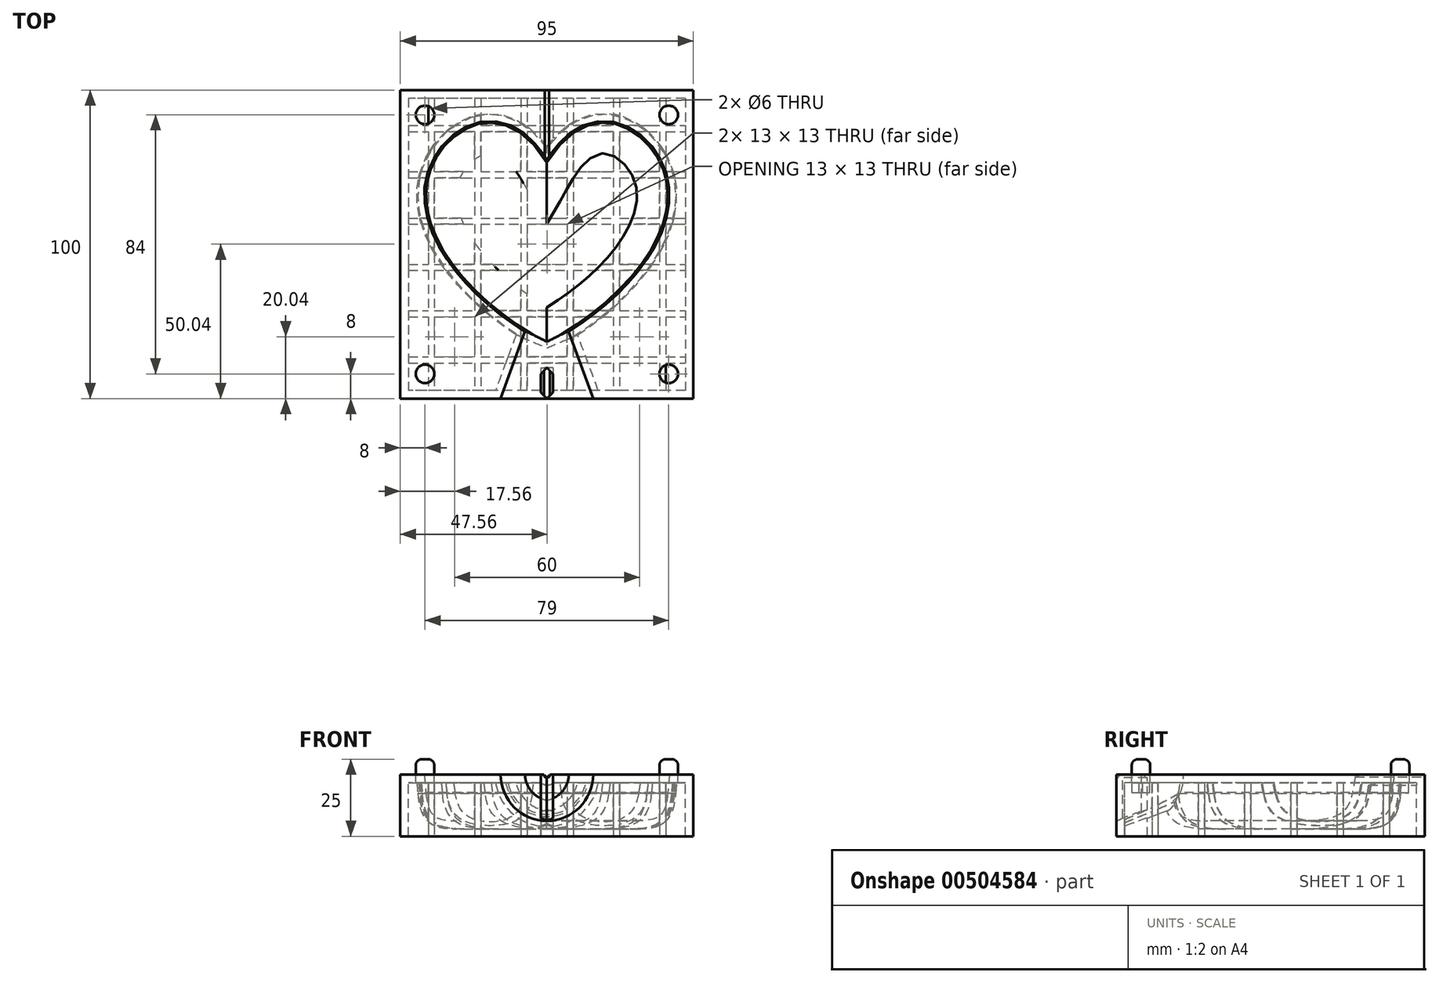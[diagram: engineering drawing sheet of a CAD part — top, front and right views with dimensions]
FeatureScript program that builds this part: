
annotation { "Feature Type Name" : "Feature", "Feature Type Description" : "" }
export const myFeature = defineFeature(function(context is Context, id is Id, definition is map)
    precondition{}
    {
        {
            var Q0;
            Q0=qCreatedBy(makeId("Top.planeOp"),FACE);
            var sketch = newSketch(context, id + "F0", { "sketchPlane" : qUnion([Q0])});
            skLineSegment(sketch, "E0", {"start": v(0, -25) * mm, "end": v(0, -81) * mm});
            skFitSpline(sketch, "E1", {"points": [v(0, -25) * mm, v(37.2, -26.59) * mm, v(0, -81) * mm], "startDerivative": vector(94.86, 165.83) * mm, "endDerivative": vector(-129.77, -70.47) * mm});
            skFitSpline(sketch, "E2.MirrorCS", {"points": [v(0, -25) * mm, v(-37.2, -26.59) * mm, v(0, -81) * mm], "startDerivative": vector(-94.86, 165.83) * mm, "endDerivative": vector(129.77, -70.47) * mm});
            skSolve(sketch);
        }
        {
            var Q0;
            Q0=makeQuery(id+"F0.imprint","IMPRINT",FACE,{"disambiguationData":[TD([[makeQuery(id+"F0.imprint","IMPRINT",EDGE,{"derivedFrom":sQuery(id+"F0.wireOp",EDGE,"E0")}),1.0]])]});
            var Q1;
            Q1=makeQuery(id+"F0.imprint","IMPRINT",FACE,{"disambiguationData":[TD([[makeQuery(id+"F0.imprint","IMPRINT",EDGE,{"derivedFrom":sQuery(id+"F0.wireOp",EDGE,"E0")}),-1.0]])]});
            extrude(context, id + "F1", {"entities" : qUnion([Q0, Q1]), "depth" : 30 * mm, "hasDraft" : true, "draftAngle" : 5 * degree});
        }
        {
            var Q0;
            Q0=makeQuery(id+"F1.opExtrude","CAP_FACE",FACE,{"disambiguationData":[OSD([sQuery(id+"F0.wireOp",EDGE,"E1"),sQuery(id+"F0.wireOp",EDGE,"E2.MirrorCS")])],"isStart":true});
            fillet(context, id + "F2", {"entities" : qUnion([Q0]), "radius" : 10 * mm, "tangentPropagation" : true, "rho" : 0.6, "crossSection" : FilletCrossSection.CONIC, "allowEdgeOverflow" : false});
        }
        {
            var Q0;
            Q0=makeQuery(id+"F1.opExtrude","CAP_FACE",FACE,{"disambiguationData":[OSD([sQuery(id+"F0.wireOp",EDGE,"E1"),sQuery(id+"F0.wireOp",EDGE,"E2.MirrorCS")])],"isStart":false});
            fillet(context, id + "F3", {"entities" : qUnion([Q0]), "radius" : 10 * mm, "tangentPropagation" : true, "rho" : 0.6, "crossSection" : FilletCrossSection.CONIC, "allowEdgeOverflow" : false});
        }
        {
            var Q0;
            Q0=qCreatedBy(makeId("Front.planeOp"),FACE);
            var sketch = newSketch(context, id + "F4", { "sketchPlane" : qUnion([Q0])});
            skCircle(sketch, "E3", {"center": v(0, 15) * mm, "radius": 0.75 * mm});
            skSolve(sketch);
        }
        {
            var Q0;
            Q0=qSketchRegion(id+"F4",true);
            extrude(context, id + "F5", {"entities" : qUnion([Q0]), "operationType" : NewBodyOperationType.ADD, "depth" : 100 * mm});
        }
        {
            var Q0;
            Q0=makeQuery(id+"F5.opExtrude","CAP_FACE",FACE,{"disambiguationData":[OSD([sQuery(id+"F4.wireOp",EDGE,"E3")])],"isStart":false});
            var sketch = newSketch(context, id + "F6", { "sketchPlane" : qUnion([Q0])});
            skCircle(sketch, "E4", {"center": v(0, 15) * mm, "radius": 15 * mm});
            skSolve(sketch);
        }
        {
            var Q0;
            Q0=makeQuery(id+"F6.imprint","IMPRINT",FACE,{"disambiguationData":[TD([[makeQuery(id+"F6.imprint","IMPRINT",EDGE,{"derivedFrom":makeQuery(id+"F5.opExtrude","CAP_EDGE",EDGE,{"disambiguationData":[OSD([sQuery(id+"F4.wireOp",EDGE,"E3")])],"isStart":false})}),1.0]])]});
            var Q1;
            Q1=makeQuery(id+"F6.imprint","IMPRINT",FACE,{"disambiguationData":[TD([[makeQuery(id+"F6.imprint","IMPRINT",EDGE,{"derivedFrom":sQuery(id+"F6.wireOp",EDGE,"E4")}),1.0]])]});
            extrude(context, id + "F7", {"entities" : qUnion([Q0, Q1]), "operationType" : NewBodyOperationType.ADD, "oppositeDirection" : true, "depth" : 60 * mm, "hasDraft" : true, "draftAngle" : 20 * degree, "draftPullDirection" : true});
        }
        {
            var Q0;
            Q0=qCreatedBy(makeId("Top.planeOp"),FACE);
            cPlane(context, id + "F8", {"entities" : qUnion([Q0]), "cplaneType" : CPlaneType.OFFSET, "offset" : 15 * mm, "width" : 150 * mm, "height" : 150 * mm});
        }
        {
            var Q0;
            Q0=qCreatedBy(id+"F8.planeOp",FACE);
            var sketch = newSketch(context, id + "F9", { "sketchPlane" : qUnion([Q0])});
            skLineSegment(sketch, "E5.bottom", {"start": v(47.5, 0) * mm, "end": v(-47.5, 0) * mm});
            skLineSegment(sketch, "E5.top", {"start": v(47.5, -100) * mm, "end": v(-47.5, -100) * mm});
            skLineSegment(sketch, "E5.left", {"start": v(47.5, 0) * mm, "end": v(47.5, -100) * mm});
            skLineSegment(sketch, "E5.right", {"start": v(-47.5, 0) * mm, "end": v(-47.5, -100) * mm});
            skPoint(sketch, "E5.middle", {"position": v(0, -50) * mm});
            skSolve(sketch);
        }
        {
            var Q0;
            Q0=qSketchRegion(id+"F9",true);
            extrude(context, id + "F10", {"entities" : qUnion([Q0]), "oppositeDirection" : true, "depth" : 20 * mm});
        }
        {
            var Q0;
            Q0=makeQuery(id+"F1.opExtrude","SWEPT_BODY",BODY,{"disambiguationData":[OSD([sQuery(id+"F0.wireOp",EDGE,"E1"),sQuery(id+"F0.wireOp",EDGE,"E2.MirrorCS")])]});
            var Q1;
            Q1=makeQuery(id+"F10.opExtrude","SWEPT_BODY",BODY,{"disambiguationData":[OSD([sQuery(id+"F9.wireOp",EDGE,"E5.bottom"),sQuery(id+"F9.wireOp",EDGE,"E5.top"),sQuery(id+"F9.wireOp",EDGE,"E5.left"),sQuery(id+"F9.wireOp",EDGE,"E5.right")])]});
            booleanBodies(context, id + "F11", {"operationType" : BooleanOperationType.SUBTRACTION, "tools" : qUnion([Q0]), "targets" : qUnion([Q1])});
        }
        {
            var Q0;
            Q0=makeQuery(id+"F10.opExtrude","CAP_FACE",FACE,{"disambiguationData":[OSD([sQuery(id+"F9.wireOp",EDGE,"E5.bottom"),sQuery(id+"F9.wireOp",EDGE,"E5.top"),sQuery(id+"F9.wireOp",EDGE,"E5.left"),sQuery(id+"F9.wireOp",EDGE,"E5.right")])],"isStart":false});
            shell(context, id + "F12", {"entities" : qUnion([Q0]), "thickness" : (0.44 * 6) * mm});
        }
        {
            var Q0;
            Q0=makeQuery(id+"F10.opExtrude","CAP_FACE",FACE,{"disambiguationData":[OSD([sQuery(id+"F9.wireOp",EDGE,"E5.bottom"),sQuery(id+"F9.wireOp",EDGE,"E5.top"),sQuery(id+"F9.wireOp",EDGE,"E5.left"),sQuery(id+"F9.wireOp",EDGE,"E5.right")])],"isStart":false});
            var sketch = newSketch(context, id + "F13", { "sketchPlane" : qUnion([Q0])});
            skLineSegment(sketch, "E6.bottom", {"start": v(38.56, 2.64) * mm, "end": v(36.56, 2.64) * mm});
            skLineSegment(sketch, "E6.top", {"start": v(38.56, 97.36) * mm, "end": v(36.56, 97.36) * mm});
            skLineSegment(sketch, "E6.left", {"start": v(38.56, 2.64) * mm, "end": v(38.56, 97.36) * mm});
            skLineSegment(sketch, "E6.right", {"start": v(36.56, 2.64) * mm, "end": v(36.56, 97.36) * mm});
            skLineSegment(sketch, "E7.1.0.0", {"start": v(23.56, 2.64) * mm, "end": v(23.56, 97.36) * mm});
            skLineSegment(sketch, "E7.1.0.1", {"start": v(21.56, 2.64) * mm, "end": v(21.56, 97.36) * mm});
            skLineSegment(sketch, "E7.1.0.2", {"start": v(23.56, 97.36) * mm, "end": v(21.56, 97.36) * mm});
            skLineSegment(sketch, "E7.1.0.3", {"start": v(23.56, 2.64) * mm, "end": v(21.56, 2.64) * mm});
            skLineSegment(sketch, "E7.2.0.0", {"start": v(8.56, 2.64) * mm, "end": v(8.56, 97.36) * mm});
            skLineSegment(sketch, "E7.2.0.1", {"start": v(6.56, 2.64) * mm, "end": v(6.56, 97.36) * mm});
            skLineSegment(sketch, "E7.2.0.2", {"start": v(8.56, 97.36) * mm, "end": v(6.56, 97.36) * mm});
            skLineSegment(sketch, "E7.2.0.3", {"start": v(8.56, 2.64) * mm, "end": v(6.56, 2.64) * mm});
            skLineSegment(sketch, "E7.3.0.0", {"start": v(-6.44, 2.64) * mm, "end": v(-6.44, 97.36) * mm});
            skLineSegment(sketch, "E7.3.0.1", {"start": v(-8.44, 2.64) * mm, "end": v(-8.44, 97.36) * mm});
            skLineSegment(sketch, "E7.3.0.2", {"start": v(-6.44, 97.36) * mm, "end": v(-8.44, 97.36) * mm});
            skLineSegment(sketch, "E7.3.0.3", {"start": v(-6.44, 2.64) * mm, "end": v(-8.44, 2.64) * mm});
            skLineSegment(sketch, "E7.4.0.0", {"start": v(-21.44, 2.64) * mm, "end": v(-21.44, 97.36) * mm});
            skLineSegment(sketch, "E7.4.0.1", {"start": v(-23.44, 2.64) * mm, "end": v(-23.44, 97.36) * mm});
            skLineSegment(sketch, "E7.4.0.2", {"start": v(-21.44, 97.36) * mm, "end": v(-23.44, 97.36) * mm});
            skLineSegment(sketch, "E7.4.0.3", {"start": v(-21.44, 2.64) * mm, "end": v(-23.44, 2.64) * mm});
            skLineSegment(sketch, "E7.5.0.0", {"start": v(-36.44, 2.64) * mm, "end": v(-36.44, 97.36) * mm});
            skLineSegment(sketch, "E7.5.0.1", {"start": v(-38.44, 2.64) * mm, "end": v(-38.44, 97.36) * mm});
            skLineSegment(sketch, "E7.5.0.2", {"start": v(-36.44, 97.36) * mm, "end": v(-38.44, 97.36) * mm});
            skLineSegment(sketch, "E7.5.0.3", {"start": v(-36.44, 2.64) * mm, "end": v(-38.44, 2.64) * mm});
            skLineSegment(sketch, "E7.direction1", {"start": v(36.56, 2.64) * mm, "end": v(21.56, 2.64) * mm, "construction": true});
            skLineSegment(sketch, "E8", {"start": v(-6.44, 2.64) * mm, "end": v(6.56, 2.64) * mm, "construction": true});
            skLineSegment(sketch, "E9.bottom", {"start": v(-44.86, 11.46) * mm, "end": v(-44.86, 13.46) * mm});
            skLineSegment(sketch, "E9.top", {"start": v(44.86, 11.46) * mm, "end": v(44.86, 13.46) * mm});
            skLineSegment(sketch, "E9.left", {"start": v(-44.86, 11.46) * mm, "end": v(44.86, 11.46) * mm});
            skLineSegment(sketch, "E9.right", {"start": v(-44.86, 13.46) * mm, "end": v(44.86, 13.46) * mm});
            skLineSegment(sketch, "E10.1.0.0", {"start": v(-44.86, 26.46) * mm, "end": v(44.86, 26.46) * mm});
            skLineSegment(sketch, "E10.1.0.1", {"start": v(-44.86, 28.46) * mm, "end": v(44.86, 28.46) * mm});
            skLineSegment(sketch, "E10.1.0.2", {"start": v(44.86, 26.46) * mm, "end": v(44.86, 28.46) * mm});
            skLineSegment(sketch, "E10.1.0.3", {"start": v(-44.86, 26.46) * mm, "end": v(-44.86, 28.46) * mm});
            skLineSegment(sketch, "E10.2.0.0", {"start": v(-44.86, 41.46) * mm, "end": v(44.86, 41.46) * mm});
            skLineSegment(sketch, "E10.2.0.1", {"start": v(-44.86, 43.46) * mm, "end": v(44.86, 43.46) * mm});
            skLineSegment(sketch, "E10.2.0.2", {"start": v(44.86, 41.46) * mm, "end": v(44.86, 43.46) * mm});
            skLineSegment(sketch, "E10.2.0.3", {"start": v(-44.86, 41.46) * mm, "end": v(-44.86, 43.46) * mm});
            skLineSegment(sketch, "E10.3.0.0", {"start": v(-44.86, 56.46) * mm, "end": v(44.86, 56.46) * mm});
            skLineSegment(sketch, "E10.3.0.1", {"start": v(-44.86, 58.46) * mm, "end": v(44.86, 58.46) * mm});
            skLineSegment(sketch, "E10.3.0.2", {"start": v(44.86, 56.46) * mm, "end": v(44.86, 58.46) * mm});
            skLineSegment(sketch, "E10.3.0.3", {"start": v(-44.86, 56.46) * mm, "end": v(-44.86, 58.46) * mm});
            skLineSegment(sketch, "E10.4.0.0", {"start": v(-44.86, 71.46) * mm, "end": v(44.86, 71.46) * mm});
            skLineSegment(sketch, "E10.4.0.1", {"start": v(-44.86, 73.46) * mm, "end": v(44.86, 73.46) * mm});
            skLineSegment(sketch, "E10.4.0.2", {"start": v(44.86, 71.46) * mm, "end": v(44.86, 73.46) * mm});
            skLineSegment(sketch, "E10.4.0.3", {"start": v(-44.86, 71.46) * mm, "end": v(-44.86, 73.46) * mm});
            skLineSegment(sketch, "E10.5.0.0", {"start": v(-44.86, 86.46) * mm, "end": v(44.86, 86.46) * mm});
            skLineSegment(sketch, "E10.5.0.1", {"start": v(-44.86, 88.46) * mm, "end": v(44.86, 88.46) * mm});
            skLineSegment(sketch, "E10.5.0.2", {"start": v(44.86, 86.46) * mm, "end": v(44.86, 88.46) * mm});
            skLineSegment(sketch, "E10.5.0.3", {"start": v(-44.86, 86.46) * mm, "end": v(-44.86, 88.46) * mm});
            skLineSegment(sketch, "E10.direction1", {"start": v(-44.86, 13.46) * mm, "end": v(-44.86, 28.46) * mm, "construction": true});
            skLineSegment(sketch, "E11", {"start": v(-44.86, 56.46) * mm, "end": v(-44.86, 43.46) * mm, "construction": true});
            skSolve(sketch);
        }
        {
            var Q0;
            Q0=makeQuery(id+"F13.imprint","IMPRINT",FACE,{"disambiguationData":[TD([[makeQuery(id+"F13.imprint","IMPRINT",EDGE,{"derivedFrom":sQuery(id+"F13.wireOp",EDGE,"E6.bottom")}),-1.0]])]});
            var Q1;
            Q1=makeQuery(id+"F13.imprint","IMPRINT",FACE,{"disambiguationData":[TD([[makeQuery(id+"F13.imprint","IMPRINT",EDGE,{"derivedFrom":sQuery(id+"F13.wireOp",EDGE,"E7.2.0.0")}),1.0]])]});
            var Q2;
            Q2=makeQuery(id+"F13.imprint","IMPRINT",FACE,{"disambiguationData":[TD([[makeQuery(id+"F13.imprint","IMPRINT",EDGE,{"derivedFrom":sQuery(id+"F13.wireOp",EDGE,"E7.3.0.0")}),1.0]])]});
            var Q3;
            Q3=makeQuery(id+"F13.imprint","IMPRINT",FACE,{"disambiguationData":[TD([[makeQuery(id+"F13.imprint","IMPRINT",EDGE,{"derivedFrom":sQuery(id+"F13.wireOp",EDGE,"E7.4.0.0")}),1.0]])]});
            var Q4;
            Q4=makeQuery(id+"F13.imprint","IMPRINT",FACE,{"disambiguationData":[TD([[makeQuery(id+"F13.imprint","IMPRINT",EDGE,{"derivedFrom":sQuery(id+"F13.wireOp",EDGE,"E7.5.0.0")}),1.0]])]});
            var Q5;
            Q5=makeQuery(id+"F13.imprint","IMPRINT",FACE,{"disambiguationData":[TD([[makeQuery(id+"F13.imprint","IMPRINT",EDGE,{"derivedFrom":sQuery(id+"F13.wireOp",EDGE,"E7.1.0.0")}),1.0]])]});
            var Q6;
            {var subQ0=sQuery(id+"F13.wireOp",EDGE,"E9.right");var subQ1=sQuery(id+"F13.wireOp",EDGE,"E6.left");var subQ2=makeQuery(id+"F13.imprint","INTERSECT",VERTEX,{"derivedFrom":[subQ1,subQ0]});Q6=makeQuery(id+"F13.imprint","IMPRINT",FACE,{"disambiguationData":[TD([[makeQuery(id+"F13.imprint","IMPRINT",EDGE,{"disambiguationData":[TD([[subQ2,-1.0]])],"derivedFrom":subQ1}),1.0]])]});}
            var Q7;
            {var subQ0=sQuery(id+"F13.wireOp",EDGE,"E10.1.0.1");var subQ1=sQuery(id+"F13.wireOp",EDGE,"E6.left");var subQ2=makeQuery(id+"F13.imprint","INTERSECT",VERTEX,{"derivedFrom":[subQ1,subQ0]});Q7=makeQuery(id+"F13.imprint","IMPRINT",FACE,{"disambiguationData":[TD([[makeQuery(id+"F13.imprint","IMPRINT",EDGE,{"disambiguationData":[TD([[subQ2,-1.0]])],"derivedFrom":subQ1}),1.0]])]});}
            var Q8;
            {var subQ0=sQuery(id+"F13.wireOp",EDGE,"E10.2.0.1");var subQ1=sQuery(id+"F13.wireOp",EDGE,"E6.left");var subQ2=makeQuery(id+"F13.imprint","INTERSECT",VERTEX,{"derivedFrom":[subQ1,subQ0]});Q8=makeQuery(id+"F13.imprint","IMPRINT",FACE,{"disambiguationData":[TD([[makeQuery(id+"F13.imprint","IMPRINT",EDGE,{"disambiguationData":[TD([[subQ2,-1.0]])],"derivedFrom":subQ1}),1.0]])]});}
            var Q9;
            {var subQ0=sQuery(id+"F13.wireOp",EDGE,"E10.1.0.0");var subQ1=sQuery(id+"F13.wireOp",EDGE,"E6.left");var subQ2=makeQuery(id+"F13.imprint","INTERSECT",VERTEX,{"derivedFrom":[subQ1,subQ0]});Q9=makeQuery(id+"F13.imprint","IMPRINT",FACE,{"disambiguationData":[TD([[makeQuery(id+"F13.imprint","IMPRINT",EDGE,{"disambiguationData":[TD([[subQ2,-1.0]])],"derivedFrom":subQ1}),1.0]])]});}
            var Q10;
            {var subQ0=sQuery(id+"F13.wireOp",EDGE,"E10.2.0.0");var subQ1=sQuery(id+"F13.wireOp",EDGE,"E6.left");var subQ2=makeQuery(id+"F13.imprint","INTERSECT",VERTEX,{"derivedFrom":[subQ1,subQ0]});Q10=makeQuery(id+"F13.imprint","IMPRINT",FACE,{"disambiguationData":[TD([[makeQuery(id+"F13.imprint","IMPRINT",EDGE,{"disambiguationData":[TD([[subQ2,-1.0]])],"derivedFrom":subQ1}),1.0]])]});}
            var Q11;
            {var subQ0=sQuery(id+"F13.wireOp",EDGE,"E10.3.0.0");var subQ1=sQuery(id+"F13.wireOp",EDGE,"E6.left");var subQ2=makeQuery(id+"F13.imprint","INTERSECT",VERTEX,{"derivedFrom":[subQ1,subQ0]});Q11=makeQuery(id+"F13.imprint","IMPRINT",FACE,{"disambiguationData":[TD([[makeQuery(id+"F13.imprint","IMPRINT",EDGE,{"disambiguationData":[TD([[subQ2,-1.0]])],"derivedFrom":subQ1}),1.0]])]});}
            var Q12;
            {var subQ0=sQuery(id+"F13.wireOp",EDGE,"E10.3.0.1");var subQ1=sQuery(id+"F13.wireOp",EDGE,"E6.left");var subQ2=makeQuery(id+"F13.imprint","INTERSECT",VERTEX,{"derivedFrom":[subQ1,subQ0]});Q12=makeQuery(id+"F13.imprint","IMPRINT",FACE,{"disambiguationData":[TD([[makeQuery(id+"F13.imprint","IMPRINT",EDGE,{"disambiguationData":[TD([[subQ2,-1.0]])],"derivedFrom":subQ1}),1.0]])]});}
            var Q13;
            {var subQ0=sQuery(id+"F13.wireOp",EDGE,"E10.4.0.0");var subQ1=sQuery(id+"F13.wireOp",EDGE,"E6.left");var subQ2=makeQuery(id+"F13.imprint","INTERSECT",VERTEX,{"derivedFrom":[subQ1,subQ0]});Q13=makeQuery(id+"F13.imprint","IMPRINT",FACE,{"disambiguationData":[TD([[makeQuery(id+"F13.imprint","IMPRINT",EDGE,{"disambiguationData":[TD([[subQ2,-1.0]])],"derivedFrom":subQ1}),1.0]])]});}
            var Q14;
            {var subQ0=sQuery(id+"F13.wireOp",EDGE,"E10.4.0.1");var subQ1=sQuery(id+"F13.wireOp",EDGE,"E6.left");var subQ2=makeQuery(id+"F13.imprint","INTERSECT",VERTEX,{"derivedFrom":[subQ1,subQ0]});Q14=makeQuery(id+"F13.imprint","IMPRINT",FACE,{"disambiguationData":[TD([[makeQuery(id+"F13.imprint","IMPRINT",EDGE,{"disambiguationData":[TD([[subQ2,-1.0]])],"derivedFrom":subQ1}),1.0]])]});}
            var Q15;
            {var subQ0=sQuery(id+"F13.wireOp",EDGE,"E6.top");Q15=makeQuery(id+"F13.imprint","IMPRINT",FACE,{"disambiguationData":[TD([[makeQuery(id+"F13.imprint","IMPRINT",EDGE,{"derivedFrom":subQ0}),1.0]])]});}
            var Q16;
            {var subQ0=sQuery(id+"F13.wireOp",EDGE,"E10.5.0.0");var subQ1=sQuery(id+"F13.wireOp",EDGE,"E6.left");var subQ2=makeQuery(id+"F13.imprint","INTERSECT",VERTEX,{"derivedFrom":[subQ1,subQ0]});Q16=makeQuery(id+"F13.imprint","IMPRINT",FACE,{"disambiguationData":[TD([[makeQuery(id+"F13.imprint","IMPRINT",EDGE,{"disambiguationData":[TD([[subQ2,-1.0]])],"derivedFrom":subQ1}),1.0]])]});}
            var Q17;
            {var subQ0=sQuery(id+"F13.wireOp",EDGE,"E9.left");var subQ1=sQuery(id+"F13.wireOp",EDGE,"E6.left");var subQ2=makeQuery(id+"F13.imprint","INTERSECT",VERTEX,{"derivedFrom":[subQ1,subQ0]});Q17=makeQuery(id+"F13.imprint","IMPRINT",FACE,{"disambiguationData":[TD([[makeQuery(id+"F13.imprint","IMPRINT",EDGE,{"disambiguationData":[TD([[subQ2,-1.0]])],"derivedFrom":subQ1}),1.0]])]});}
            var Q18;
            {var subQ0=sQuery(id+"F13.wireOp",EDGE,"E9.left");var subQ1=sQuery(id+"F13.wireOp",EDGE,"E6.left");var subQ2=makeQuery(id+"F13.imprint","INTERSECT",VERTEX,{"derivedFrom":[subQ1,subQ0]});Q18=makeQuery(id+"F13.imprint","IMPRINT",FACE,{"disambiguationData":[TD([[makeQuery(id+"F13.imprint","IMPRINT",EDGE,{"disambiguationData":[TD([[subQ2,-1.0]])],"derivedFrom":subQ1}),1.0]])]});}
            var Q19;
            {var subQ5=sQuery(id+"F13.wireOp",EDGE,"E9.top");Q19=makeQuery(id+"F13.imprint","IMPRINT",FACE,{"disambiguationData":[TD([[makeQuery(id+"F13.imprint","IMPRINT",EDGE,{"derivedFrom":subQ5}),1.0]])]});}
            var Q20;
            {var subQ0=sQuery(id+"F13.wireOp",EDGE,"E9.left");var subQ1=sQuery(id+"F13.wireOp",EDGE,"E6.right");var subQ2=makeQuery(id+"F13.imprint","INTERSECT",VERTEX,{"derivedFrom":[subQ1,subQ0]});Q20=makeQuery(id+"F13.imprint","IMPRINT",FACE,{"disambiguationData":[TD([[makeQuery(id+"F13.imprint","IMPRINT",EDGE,{"disambiguationData":[TD([[subQ2,-1.0]])],"derivedFrom":subQ1}),1.0]])]});}
            var Q21;
            {var subQ0=sQuery(id+"F13.wireOp",EDGE,"E9.left");var subQ1=sQuery(id+"F13.wireOp",EDGE,"E7.1.0.1");var subQ2=makeQuery(id+"F13.imprint","INTERSECT",VERTEX,{"derivedFrom":[subQ1,subQ0]});Q21=makeQuery(id+"F13.imprint","IMPRINT",FACE,{"disambiguationData":[TD([[makeQuery(id+"F13.imprint","IMPRINT",EDGE,{"disambiguationData":[TD([[subQ2,-1.0]])],"derivedFrom":subQ1}),1.0]])]});}
            var Q22;
            {var subQ0=sQuery(id+"F13.wireOp",EDGE,"E9.left");var subQ1=sQuery(id+"F13.wireOp",EDGE,"E7.2.0.1");var subQ2=makeQuery(id+"F13.imprint","INTERSECT",VERTEX,{"derivedFrom":[subQ1,subQ0]});Q22=makeQuery(id+"F13.imprint","IMPRINT",FACE,{"disambiguationData":[TD([[makeQuery(id+"F13.imprint","IMPRINT",EDGE,{"disambiguationData":[TD([[subQ2,-1.0]])],"derivedFrom":subQ1}),1.0]])]});}
            var Q23;
            {var subQ0=sQuery(id+"F13.wireOp",EDGE,"E10.3.0.0");var subQ1=sQuery(id+"F13.wireOp",EDGE,"E7.2.0.1");var subQ2=makeQuery(id+"F13.imprint","INTERSECT",VERTEX,{"derivedFrom":[subQ1,subQ0]});Q23=makeQuery(id+"F13.imprint","IMPRINT",FACE,{"disambiguationData":[TD([[makeQuery(id+"F13.imprint","IMPRINT",EDGE,{"disambiguationData":[TD([[subQ2,-1.0]])],"derivedFrom":subQ1}),1.0]])]});}
            var Q24;
            {var subQ0=sQuery(id+"F13.wireOp",EDGE,"E10.3.0.0");var subQ1=sQuery(id+"F13.wireOp",EDGE,"E7.1.0.1");var subQ2=makeQuery(id+"F13.imprint","INTERSECT",VERTEX,{"derivedFrom":[subQ1,subQ0]});Q24=makeQuery(id+"F13.imprint","IMPRINT",FACE,{"disambiguationData":[TD([[makeQuery(id+"F13.imprint","IMPRINT",EDGE,{"disambiguationData":[TD([[subQ2,-1.0]])],"derivedFrom":subQ1}),1.0]])]});}
            var Q25;
            {var subQ0=sQuery(id+"F13.wireOp",EDGE,"E10.2.0.0");var subQ1=sQuery(id+"F13.wireOp",EDGE,"E7.1.0.1");var subQ2=makeQuery(id+"F13.imprint","INTERSECT",VERTEX,{"derivedFrom":[subQ1,subQ0]});Q25=makeQuery(id+"F13.imprint","IMPRINT",FACE,{"disambiguationData":[TD([[makeQuery(id+"F13.imprint","IMPRINT",EDGE,{"disambiguationData":[TD([[subQ2,-1.0]])],"derivedFrom":subQ1}),1.0]])]});}
            var Q26;
            {var subQ0=sQuery(id+"F13.wireOp",EDGE,"E10.1.0.0");var subQ1=sQuery(id+"F13.wireOp",EDGE,"E7.1.0.1");var subQ2=makeQuery(id+"F13.imprint","INTERSECT",VERTEX,{"derivedFrom":[subQ1,subQ0]});Q26=makeQuery(id+"F13.imprint","IMPRINT",FACE,{"disambiguationData":[TD([[makeQuery(id+"F13.imprint","IMPRINT",EDGE,{"disambiguationData":[TD([[subQ2,-1.0]])],"derivedFrom":subQ1}),1.0]])]});}
            var Q27;
            {var subQ0=sQuery(id+"F13.wireOp",EDGE,"E10.1.0.0");var subQ1=sQuery(id+"F13.wireOp",EDGE,"E6.right");var subQ2=makeQuery(id+"F13.imprint","INTERSECT",VERTEX,{"derivedFrom":[subQ1,subQ0]});Q27=makeQuery(id+"F13.imprint","IMPRINT",FACE,{"disambiguationData":[TD([[makeQuery(id+"F13.imprint","IMPRINT",EDGE,{"disambiguationData":[TD([[subQ2,-1.0]])],"derivedFrom":subQ1}),1.0]])]});}
            var Q28;
            {var subQ0=sQuery(id+"F13.wireOp",EDGE,"E10.2.0.0");var subQ1=sQuery(id+"F13.wireOp",EDGE,"E6.right");var subQ2=makeQuery(id+"F13.imprint","INTERSECT",VERTEX,{"derivedFrom":[subQ1,subQ0]});Q28=makeQuery(id+"F13.imprint","IMPRINT",FACE,{"disambiguationData":[TD([[makeQuery(id+"F13.imprint","IMPRINT",EDGE,{"disambiguationData":[TD([[subQ2,-1.0]])],"derivedFrom":subQ1}),1.0]])]});}
            var Q29;
            {var subQ5=sQuery(id+"F13.wireOp",EDGE,"E10.2.0.2");Q29=makeQuery(id+"F13.imprint","IMPRINT",FACE,{"disambiguationData":[TD([[makeQuery(id+"F13.imprint","IMPRINT",EDGE,{"derivedFrom":subQ5}),1.0]])]});}
            var Q30;
            {var subQ5=sQuery(id+"F13.wireOp",EDGE,"E10.3.0.2");Q30=makeQuery(id+"F13.imprint","IMPRINT",FACE,{"disambiguationData":[TD([[makeQuery(id+"F13.imprint","IMPRINT",EDGE,{"derivedFrom":subQ5}),1.0]])]});}
            var Q31;
            {var subQ0=sQuery(id+"F13.wireOp",EDGE,"E10.3.0.0");var subQ1=sQuery(id+"F13.wireOp",EDGE,"E6.right");var subQ2=makeQuery(id+"F13.imprint","INTERSECT",VERTEX,{"derivedFrom":[subQ1,subQ0]});Q31=makeQuery(id+"F13.imprint","IMPRINT",FACE,{"disambiguationData":[TD([[makeQuery(id+"F13.imprint","IMPRINT",EDGE,{"disambiguationData":[TD([[subQ2,-1.0]])],"derivedFrom":subQ1}),1.0]])]});}
            var Q32;
            {var subQ0=sQuery(id+"F13.wireOp",EDGE,"E9.left");var subQ1=sQuery(id+"F13.wireOp",EDGE,"E7.4.0.1");var subQ2=makeQuery(id+"F13.imprint","INTERSECT",VERTEX,{"derivedFrom":[subQ1,subQ0]});Q32=makeQuery(id+"F13.imprint","IMPRINT",FACE,{"disambiguationData":[TD([[makeQuery(id+"F13.imprint","IMPRINT",EDGE,{"disambiguationData":[TD([[subQ2,-1.0]])],"derivedFrom":subQ1}),1.0]])]});}
            var Q33;
            {var subQ5=sQuery(id+"F13.wireOp",EDGE,"E9.bottom");Q33=makeQuery(id+"F13.imprint","IMPRINT",FACE,{"disambiguationData":[TD([[makeQuery(id+"F13.imprint","IMPRINT",EDGE,{"derivedFrom":subQ5}),-1.0]])]});}
            var Q34;
            {var subQ0=sQuery(id+"F13.wireOp",EDGE,"E9.left");var subQ1=sQuery(id+"F13.wireOp",EDGE,"E7.3.0.1");var subQ2=makeQuery(id+"F13.imprint","INTERSECT",VERTEX,{"derivedFrom":[subQ1,subQ0]});Q34=makeQuery(id+"F13.imprint","IMPRINT",FACE,{"disambiguationData":[TD([[makeQuery(id+"F13.imprint","IMPRINT",EDGE,{"disambiguationData":[TD([[subQ2,-1.0]])],"derivedFrom":subQ1}),1.0]])]});}
            var Q35;
            {var subQ0=sQuery(id+"F13.wireOp",EDGE,"E10.1.0.0");var subQ1=sQuery(id+"F13.wireOp",EDGE,"E7.3.0.1");var subQ2=makeQuery(id+"F13.imprint","INTERSECT",VERTEX,{"derivedFrom":[subQ1,subQ0]});Q35=makeQuery(id+"F13.imprint","IMPRINT",FACE,{"disambiguationData":[TD([[makeQuery(id+"F13.imprint","IMPRINT",EDGE,{"disambiguationData":[TD([[subQ2,-1.0]])],"derivedFrom":subQ1}),1.0]])]});}
            var Q36;
            {var subQ0=sQuery(id+"F13.wireOp",EDGE,"E10.1.0.0");var subQ1=sQuery(id+"F13.wireOp",EDGE,"E7.4.0.1");var subQ2=makeQuery(id+"F13.imprint","INTERSECT",VERTEX,{"derivedFrom":[subQ1,subQ0]});Q36=makeQuery(id+"F13.imprint","IMPRINT",FACE,{"disambiguationData":[TD([[makeQuery(id+"F13.imprint","IMPRINT",EDGE,{"disambiguationData":[TD([[subQ2,-1.0]])],"derivedFrom":subQ1}),1.0]])]});}
            var Q37;
            {var subQ5=sQuery(id+"F13.wireOp",EDGE,"E10.1.0.3");Q37=makeQuery(id+"F13.imprint","IMPRINT",FACE,{"disambiguationData":[TD([[makeQuery(id+"F13.imprint","IMPRINT",EDGE,{"derivedFrom":subQ5}),-1.0]])]});}
            var Q38;
            {var subQ5=sQuery(id+"F13.wireOp",EDGE,"E10.2.0.3");Q38=makeQuery(id+"F13.imprint","IMPRINT",FACE,{"disambiguationData":[TD([[makeQuery(id+"F13.imprint","IMPRINT",EDGE,{"derivedFrom":subQ5}),-1.0]])]});}
            var Q39;
            {var subQ0=sQuery(id+"F13.wireOp",EDGE,"E10.2.0.0");var subQ1=sQuery(id+"F13.wireOp",EDGE,"E7.4.0.1");var subQ2=makeQuery(id+"F13.imprint","INTERSECT",VERTEX,{"derivedFrom":[subQ1,subQ0]});Q39=makeQuery(id+"F13.imprint","IMPRINT",FACE,{"disambiguationData":[TD([[makeQuery(id+"F13.imprint","IMPRINT",EDGE,{"disambiguationData":[TD([[subQ2,-1.0]])],"derivedFrom":subQ1}),1.0]])]});}
            var Q40;
            {var subQ0=sQuery(id+"F13.wireOp",EDGE,"E10.2.0.0");var subQ1=sQuery(id+"F13.wireOp",EDGE,"E7.3.0.1");var subQ2=makeQuery(id+"F13.imprint","INTERSECT",VERTEX,{"derivedFrom":[subQ1,subQ0]});Q40=makeQuery(id+"F13.imprint","IMPRINT",FACE,{"disambiguationData":[TD([[makeQuery(id+"F13.imprint","IMPRINT",EDGE,{"disambiguationData":[TD([[subQ2,-1.0]])],"derivedFrom":subQ1}),1.0]])]});}
            var Q41;
            {var subQ0=sQuery(id+"F13.wireOp",EDGE,"E10.1.0.0");var subQ1=sQuery(id+"F13.wireOp",EDGE,"E7.2.0.1");var subQ2=makeQuery(id+"F13.imprint","INTERSECT",VERTEX,{"derivedFrom":[subQ1,subQ0]});Q41=makeQuery(id+"F13.imprint","IMPRINT",FACE,{"disambiguationData":[TD([[makeQuery(id+"F13.imprint","IMPRINT",EDGE,{"disambiguationData":[TD([[subQ2,-1.0]])],"derivedFrom":subQ1}),1.0]])]});}
            var Q42;
            {var subQ0=sQuery(id+"F13.wireOp",EDGE,"E10.2.0.0");var subQ1=sQuery(id+"F13.wireOp",EDGE,"E7.2.0.1");var subQ2=makeQuery(id+"F13.imprint","INTERSECT",VERTEX,{"derivedFrom":[subQ1,subQ0]});Q42=makeQuery(id+"F13.imprint","IMPRINT",FACE,{"disambiguationData":[TD([[makeQuery(id+"F13.imprint","IMPRINT",EDGE,{"disambiguationData":[TD([[subQ2,-1.0]])],"derivedFrom":subQ1}),1.0]])]});}
            var Q43;
            {var subQ0=sQuery(id+"F13.wireOp",EDGE,"E10.4.0.0");var subQ1=sQuery(id+"F13.wireOp",EDGE,"E7.2.0.1");var subQ2=makeQuery(id+"F13.imprint","INTERSECT",VERTEX,{"derivedFrom":[subQ1,subQ0]});Q43=makeQuery(id+"F13.imprint","IMPRINT",FACE,{"disambiguationData":[TD([[makeQuery(id+"F13.imprint","IMPRINT",EDGE,{"disambiguationData":[TD([[subQ2,-1.0]])],"derivedFrom":subQ1}),1.0]])]});}
            var Q44;
            {var subQ0=sQuery(id+"F13.wireOp",EDGE,"E10.4.0.0");var subQ1=sQuery(id+"F13.wireOp",EDGE,"E7.1.0.1");var subQ2=makeQuery(id+"F13.imprint","INTERSECT",VERTEX,{"derivedFrom":[subQ1,subQ0]});Q44=makeQuery(id+"F13.imprint","IMPRINT",FACE,{"disambiguationData":[TD([[makeQuery(id+"F13.imprint","IMPRINT",EDGE,{"disambiguationData":[TD([[subQ2,-1.0]])],"derivedFrom":subQ1}),1.0]])]});}
            var Q45;
            {var subQ0=sQuery(id+"F13.wireOp",EDGE,"E10.4.0.0");var subQ1=sQuery(id+"F13.wireOp",EDGE,"E6.right");var subQ2=makeQuery(id+"F13.imprint","INTERSECT",VERTEX,{"derivedFrom":[subQ1,subQ0]});Q45=makeQuery(id+"F13.imprint","IMPRINT",FACE,{"disambiguationData":[TD([[makeQuery(id+"F13.imprint","IMPRINT",EDGE,{"disambiguationData":[TD([[subQ2,-1.0]])],"derivedFrom":subQ1}),1.0]])]});}
            var Q46;
            {var subQ5=sQuery(id+"F13.wireOp",EDGE,"E10.4.0.2");Q46=makeQuery(id+"F13.imprint","IMPRINT",FACE,{"disambiguationData":[TD([[makeQuery(id+"F13.imprint","IMPRINT",EDGE,{"derivedFrom":subQ5}),1.0]])]});}
            var Q47;
            {var subQ5=sQuery(id+"F13.wireOp",EDGE,"E10.5.0.2");Q47=makeQuery(id+"F13.imprint","IMPRINT",FACE,{"disambiguationData":[TD([[makeQuery(id+"F13.imprint","IMPRINT",EDGE,{"derivedFrom":subQ5}),1.0]])]});}
            var Q48;
            {var subQ0=sQuery(id+"F13.wireOp",EDGE,"E10.5.0.0");var subQ1=sQuery(id+"F13.wireOp",EDGE,"E6.right");var subQ2=makeQuery(id+"F13.imprint","INTERSECT",VERTEX,{"derivedFrom":[subQ1,subQ0]});Q48=makeQuery(id+"F13.imprint","IMPRINT",FACE,{"disambiguationData":[TD([[makeQuery(id+"F13.imprint","IMPRINT",EDGE,{"disambiguationData":[TD([[subQ2,-1.0]])],"derivedFrom":subQ1}),1.0]])]});}
            var Q49;
            {var subQ0=sQuery(id+"F13.wireOp",EDGE,"E10.5.0.0");var subQ1=sQuery(id+"F13.wireOp",EDGE,"E7.1.0.1");var subQ2=makeQuery(id+"F13.imprint","INTERSECT",VERTEX,{"derivedFrom":[subQ1,subQ0]});Q49=makeQuery(id+"F13.imprint","IMPRINT",FACE,{"disambiguationData":[TD([[makeQuery(id+"F13.imprint","IMPRINT",EDGE,{"disambiguationData":[TD([[subQ2,-1.0]])],"derivedFrom":subQ1}),1.0]])]});}
            var Q50;
            {var subQ5=sQuery(id+"F13.wireOp",EDGE,"E10.3.0.3");Q50=makeQuery(id+"F13.imprint","IMPRINT",FACE,{"disambiguationData":[TD([[makeQuery(id+"F13.imprint","IMPRINT",EDGE,{"derivedFrom":subQ5}),-1.0]])]});}
            var Q51;
            {var subQ5=sQuery(id+"F13.wireOp",EDGE,"E10.4.0.3");Q51=makeQuery(id+"F13.imprint","IMPRINT",FACE,{"disambiguationData":[TD([[makeQuery(id+"F13.imprint","IMPRINT",EDGE,{"derivedFrom":subQ5}),-1.0]])]});}
            var Q52;
            {var subQ5=sQuery(id+"F13.wireOp",EDGE,"E10.5.0.3");Q52=makeQuery(id+"F13.imprint","IMPRINT",FACE,{"disambiguationData":[TD([[makeQuery(id+"F13.imprint","IMPRINT",EDGE,{"derivedFrom":subQ5}),-1.0]])]});}
            var Q53;
            {var subQ0=sQuery(id+"F13.wireOp",EDGE,"E10.5.0.0");var subQ1=sQuery(id+"F13.wireOp",EDGE,"E7.4.0.1");var subQ2=makeQuery(id+"F13.imprint","INTERSECT",VERTEX,{"derivedFrom":[subQ1,subQ0]});Q53=makeQuery(id+"F13.imprint","IMPRINT",FACE,{"disambiguationData":[TD([[makeQuery(id+"F13.imprint","IMPRINT",EDGE,{"disambiguationData":[TD([[subQ2,-1.0]])],"derivedFrom":subQ1}),1.0]])]});}
            var Q54;
            {var subQ0=sQuery(id+"F13.wireOp",EDGE,"E10.5.0.0");var subQ1=sQuery(id+"F13.wireOp",EDGE,"E7.3.0.1");var subQ2=makeQuery(id+"F13.imprint","INTERSECT",VERTEX,{"derivedFrom":[subQ1,subQ0]});Q54=makeQuery(id+"F13.imprint","IMPRINT",FACE,{"disambiguationData":[TD([[makeQuery(id+"F13.imprint","IMPRINT",EDGE,{"disambiguationData":[TD([[subQ2,-1.0]])],"derivedFrom":subQ1}),1.0]])]});}
            var Q55;
            {var subQ0=sQuery(id+"F13.wireOp",EDGE,"E10.5.0.0");var subQ1=sQuery(id+"F13.wireOp",EDGE,"E7.2.0.1");var subQ2=makeQuery(id+"F13.imprint","INTERSECT",VERTEX,{"derivedFrom":[subQ1,subQ0]});Q55=makeQuery(id+"F13.imprint","IMPRINT",FACE,{"disambiguationData":[TD([[makeQuery(id+"F13.imprint","IMPRINT",EDGE,{"disambiguationData":[TD([[subQ2,-1.0]])],"derivedFrom":subQ1}),1.0]])]});}
            var Q56;
            {var subQ0=sQuery(id+"F13.wireOp",EDGE,"E10.4.0.0");var subQ1=sQuery(id+"F13.wireOp",EDGE,"E7.3.0.1");var subQ2=makeQuery(id+"F13.imprint","INTERSECT",VERTEX,{"derivedFrom":[subQ1,subQ0]});Q56=makeQuery(id+"F13.imprint","IMPRINT",FACE,{"disambiguationData":[TD([[makeQuery(id+"F13.imprint","IMPRINT",EDGE,{"disambiguationData":[TD([[subQ2,-1.0]])],"derivedFrom":subQ1}),1.0]])]});}
            var Q57;
            {var subQ0=sQuery(id+"F13.wireOp",EDGE,"E10.4.0.0");var subQ1=sQuery(id+"F13.wireOp",EDGE,"E7.4.0.1");var subQ2=makeQuery(id+"F13.imprint","INTERSECT",VERTEX,{"derivedFrom":[subQ1,subQ0]});Q57=makeQuery(id+"F13.imprint","IMPRINT",FACE,{"disambiguationData":[TD([[makeQuery(id+"F13.imprint","IMPRINT",EDGE,{"disambiguationData":[TD([[subQ2,-1.0]])],"derivedFrom":subQ1}),1.0]])]});}
            var Q58;
            {var subQ0=sQuery(id+"F13.wireOp",EDGE,"E10.3.0.0");var subQ1=sQuery(id+"F13.wireOp",EDGE,"E7.4.0.1");var subQ2=makeQuery(id+"F13.imprint","INTERSECT",VERTEX,{"derivedFrom":[subQ1,subQ0]});Q58=makeQuery(id+"F13.imprint","IMPRINT",FACE,{"disambiguationData":[TD([[makeQuery(id+"F13.imprint","IMPRINT",EDGE,{"disambiguationData":[TD([[subQ2,-1.0]])],"derivedFrom":subQ1}),1.0]])]});}
            var Q59;
            {var subQ0=sQuery(id+"F13.wireOp",EDGE,"E10.3.0.0");var subQ1=sQuery(id+"F13.wireOp",EDGE,"E7.3.0.1");var subQ2=makeQuery(id+"F13.imprint","INTERSECT",VERTEX,{"derivedFrom":[subQ1,subQ0]});Q59=makeQuery(id+"F13.imprint","IMPRINT",FACE,{"disambiguationData":[TD([[makeQuery(id+"F13.imprint","IMPRINT",EDGE,{"disambiguationData":[TD([[subQ2,-1.0]])],"derivedFrom":subQ1}),1.0]])]});}
            var Q60;
            {var subQ5=sQuery(id+"F13.wireOp",EDGE,"E10.1.0.2");Q60=makeQuery(id+"F13.imprint","IMPRINT",FACE,{"disambiguationData":[TD([[makeQuery(id+"F13.imprint","IMPRINT",EDGE,{"derivedFrom":subQ5}),1.0]])]});}
            extrude(context, id + "F14", {"entities" : qUnion([Q0, Q1, Q2, Q3, Q4, Q5, Q6, Q7, Q8, Q9, Q10, Q11, Q12, Q13, Q14, Q15, Q16, Q17, Q18, Q19, Q20, Q21, Q22, Q23, Q24, Q25, Q26, Q27, Q28, Q29, Q30, Q31, Q32, Q33, Q34, Q35, Q36, Q37, Q38, Q39, Q40, Q41, Q42, Q43, Q44, Q45, Q46, Q47, Q48, Q49, Q50, Q51, Q52, Q53, Q54, Q55, Q56, Q57, Q58, Q59, Q60]), "endBound" : BoundingType.UP_TO_NEXT, "oppositeDirection" : true, "depth" : 25 * mm});
        }
        {
            var Q0;
            {var subQ0=sQuery(id+"F9.wireOp",EDGE,"E5.bottom");var subQ1=sQuery(id+"F9.wireOp",EDGE,"E5.top");var subQ2=sQuery(id+"F9.wireOp",EDGE,"E5.right");Q0=makeQuery(id+"F11.opBoolean","SPLIT",FACE,{"disambiguationData":[TD([makeQuery(id+"F1.opExtrude","SWEPT_FACE",FACE,{"disambiguationData":[OSD([sQuery(id+"F0.wireOp",EDGE,"E2.MirrorCS")])]})])],"derivedFrom":makeQuery(id+"F10.opExtrude","CAP_FACE",FACE,{"disambiguationData":[OSD([subQ0,subQ1,sQuery(id+"F9.wireOp",EDGE,"E5.left"),subQ2])],"isStart":true})});}
            var sketch = newSketch(context, id + "F15", { "sketchPlane" : qUnion([Q0])});
            skCircle(sketch, "E12", {"center": v(-39.5, -8) * mm, "radius": 3 * mm});
            skCircle(sketch, "E13", {"center": v(39.5, -8) * mm, "radius": 3 * mm});
            skCircle(sketch, "E14", {"center": v(39.5, -92) * mm, "radius": 3 * mm});
            skCircle(sketch, "E15", {"center": v(-39.5, -92) * mm, "radius": 3 * mm});
            skSolve(sketch);
        }
        {
            var Q0;
            Q0=makeQuery(id+"F15.imprint","IMPRINT",FACE,{"disambiguationData":[TD([[makeQuery(id+"F15.imprint","IMPRINT",EDGE,{"derivedFrom":sQuery(id+"F15.wireOp",EDGE,"E13")}),1.0]])]});
            var Q1;
            Q1=makeQuery(id+"F15.imprint","IMPRINT",FACE,{"disambiguationData":[TD([[makeQuery(id+"F15.imprint","IMPRINT",EDGE,{"derivedFrom":sQuery(id+"F15.wireOp",EDGE,"E15")}),1.0]])]});
            extrude(context, id + "F16", {"entities" : qUnion([Q0, Q1]), "operationType" : NewBodyOperationType.ADD, "depth" : 5 * mm});
        }
        {
            var Q0;
            Q0=makeQuery(id+"F15.imprint","IMPRINT",FACE,{"disambiguationData":[TD([[makeQuery(id+"F15.imprint","IMPRINT",EDGE,{"derivedFrom":sQuery(id+"F15.wireOp",EDGE,"E14")}),1.0]])]});
            var Q1;
            Q1=makeQuery(id+"F15.imprint","IMPRINT",FACE,{"disambiguationData":[TD([[makeQuery(id+"F15.imprint","IMPRINT",EDGE,{"derivedFrom":sQuery(id+"F15.wireOp",EDGE,"E12")}),1.0]])]});
            extrude(context, id + "F17", {"entities" : qUnion([Q0, Q1]), "operationType" : NewBodyOperationType.REMOVE, "oppositeDirection" : true, "depth" : 6 * mm});
        }
        {
            var Q0;
            Q0=makeQuery(id+"F16.opExtrude","CAP_EDGE",EDGE,{"disambiguationData":[OSD([sQuery(id+"F15.wireOp",EDGE,"E15")])],"isStart":false});
            fillet(context, id + "F18", {"entities" : qUnion([Q0]), "radius" : 2 * mm, "tangentPropagation" : true, "allowEdgeOverflow" : false});
        }
        {
            var Q0;
            Q0=makeQuery(id+"F16.opExtrude","CAP_EDGE",EDGE,{"disambiguationData":[OSD([sQuery(id+"F15.wireOp",EDGE,"E13")])],"isStart":false});
            fillet(context, id + "F19", {"entities" : qUnion([Q0]), "radius" : 2 * mm, "tangentPropagation" : true, "allowEdgeOverflow" : false});
        }
        {
            var Q0;
            Q0=makeQuery(id+"F10.opExtrude","SWEPT_FACE",FACE,{"disambiguationData":[OSD([sQuery(id+"F9.wireOp",EDGE,"E5.top")])]});
            var sketch = newSketch(context, id + "F20", { "sketchPlane" : qUnion([Q0])});
            skLineSegment(sketch, "E16.bottom", {"start": v(-2, -5) * mm, "end": v(2, -5) * mm});
            skLineSegment(sketch, "E16.top", {"start": v(-2, 35) * mm, "end": v(2, 35) * mm});
            skLineSegment(sketch, "E16.left", {"start": v(-2, -5) * mm, "end": v(-2, 15) * mm});
            skLineSegment(sketch, "E16.right", {"start": v(2, -5) * mm, "end": v(2, 15) * mm});
            skPoint(sketch, "E16.middle", {"position": v(0, 15) * mm});
            skLineSegment(sketch, "E17", {"start": v(2, 15) * mm, "end": v(-2, 15) * mm, "construction": true});
            skArc(sketch, "E18", {"start": v(-1, 15) * mm, "mid": v(0, 14) * mm, "end": v(1, 15) * mm});
            skLineSegment(sketch, "E19", {"start": v(2, 15) * mm, "end": v(1, 15) * mm});
            skLineSegment(sketch, "E20", {"start": v(-2, 15) * mm, "end": v(-1, 15) * mm});
            skSolve(sketch);
        }
        {
            var Q0;
            Q0 = qSketchRegion(id + "F20", true);
            extrude(context, id + "F21", {"entities" : qUnion([Q0]), "operationType" : NewBodyOperationType.ADD, "oppositeDirection" : true, "depth" : 10 * mm});
        }
        {
            var Q0;
            Q0=makeQuery(id+"F21.opExtrude","CAP_EDGE",EDGE,{"disambiguationData":[OSD([sQuery(id+"F20.wireOp",EDGE,"E16.right")])],"isStart":true});
            var Q1;
            Q1=makeQuery(id+"F21.opExtrude","CAP_EDGE",EDGE,{"disambiguationData":[OSD([sQuery(id+"F20.wireOp",EDGE,"E16.left")])],"isStart":true});
            chamfer(context, id + "F22", {"entities" : qUnion([Q0, Q1]), "width" : 2 * mm, "tangentPropagation" : true});
        }
        {
            var Q0;
            {var subQ1=sQuery(id+"F20.wireOp",EDGE,"E16.left");Q0=makeQuery(id+"F21.boolean.opBoolean","SPLIT",EDGE,{"disambiguationData":[TD([makeQuery(id+"F11.opBoolean","COPY",FACE,{"derivedFrom":makeQuery(id+"F7.opExtrude","SWEPT_FACE",FACE,{"disambiguationData":[OSD([sQuery(id+"F6.wireOp",EDGE,"E4")])]})})])],"derivedFrom":makeQuery(id+"F21.opExtrude","CAP_EDGE",EDGE,{"disambiguationData":[OSD([subQ1])],"isStart":false})});}
            var Q1;
            {var subQ0=sQuery(id+"F20.wireOp",EDGE,"E16.right");Q1=makeQuery(id+"F21.boolean.opBoolean","SPLIT",EDGE,{"disambiguationData":[TD([makeQuery(id+"F11.opBoolean","COPY",FACE,{"derivedFrom":makeQuery(id+"F7.opExtrude","SWEPT_FACE",FACE,{"disambiguationData":[OSD([sQuery(id+"F6.wireOp",EDGE,"E4")])]})})])],"derivedFrom":makeQuery(id+"F21.opExtrude","CAP_EDGE",EDGE,{"disambiguationData":[OSD([subQ0])],"isStart":false})});}
            chamfer(context, id + "F23", {"entities" : qUnion([Q0, Q1]), "width" : 2 * mm, "tangentPropagation" : true});
        }
    });
